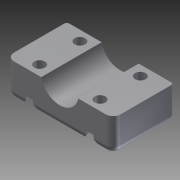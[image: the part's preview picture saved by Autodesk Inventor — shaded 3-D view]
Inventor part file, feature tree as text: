
AUTODESK INVENTOR PART (.ipt)
format: ipt  version: 2012 (Build 160160000, 160)  size: 184,832 bytes
history: native  units: mm
features: extrude x4, sketch x4, fillet x3
ambient origin geometry x8: Origin, YZ Plane, XZ Plane, XY Plane, X Axis, Y Axis, Z Axis, Center Point
bodies: Solid1 (feature_tree)
feature tree (11):
  extrude  "Extrusion1"  Depth=42.4mm
  extrude  "Extrusion2"  Depth=9.2mm
  fillet  "Fillet1"  Radius=9.2mm
  extrude  "Extrusion3"  Depth=9.2mm
  extrude  "Extrusion4"  Depth=4.0mm
  fillet  "Fillet3"  Radius=4.0mm
  fillet  "Fillet4"  Radius=4.0mm
  sketch  "Sketch1"  dims[d0=24.0mm d1=42.4mm]
  sketch  "Sketch2"  dims[d2=4.2mm d3=9.2mm d4=9.2mm]
  sketch  "Sketch3"  dims[d5=9.2mm d6=9.2mm]
  sketch  "Sketch4"  dims[d7=4.0mm d8=4.0mm d9=4.0mm d10=4.0mm d11=13.5mm d12=0.0mm d13=15.0mm d14=21.2mm d15=1.5mm d16=13.5mm d17=0.0mm d18=3.0mm d20=8.5mm d21=4.0mm d22=0.0mm d23=12.3mm d24=0.0mm d25=3.0mm d26=1.0mm]
